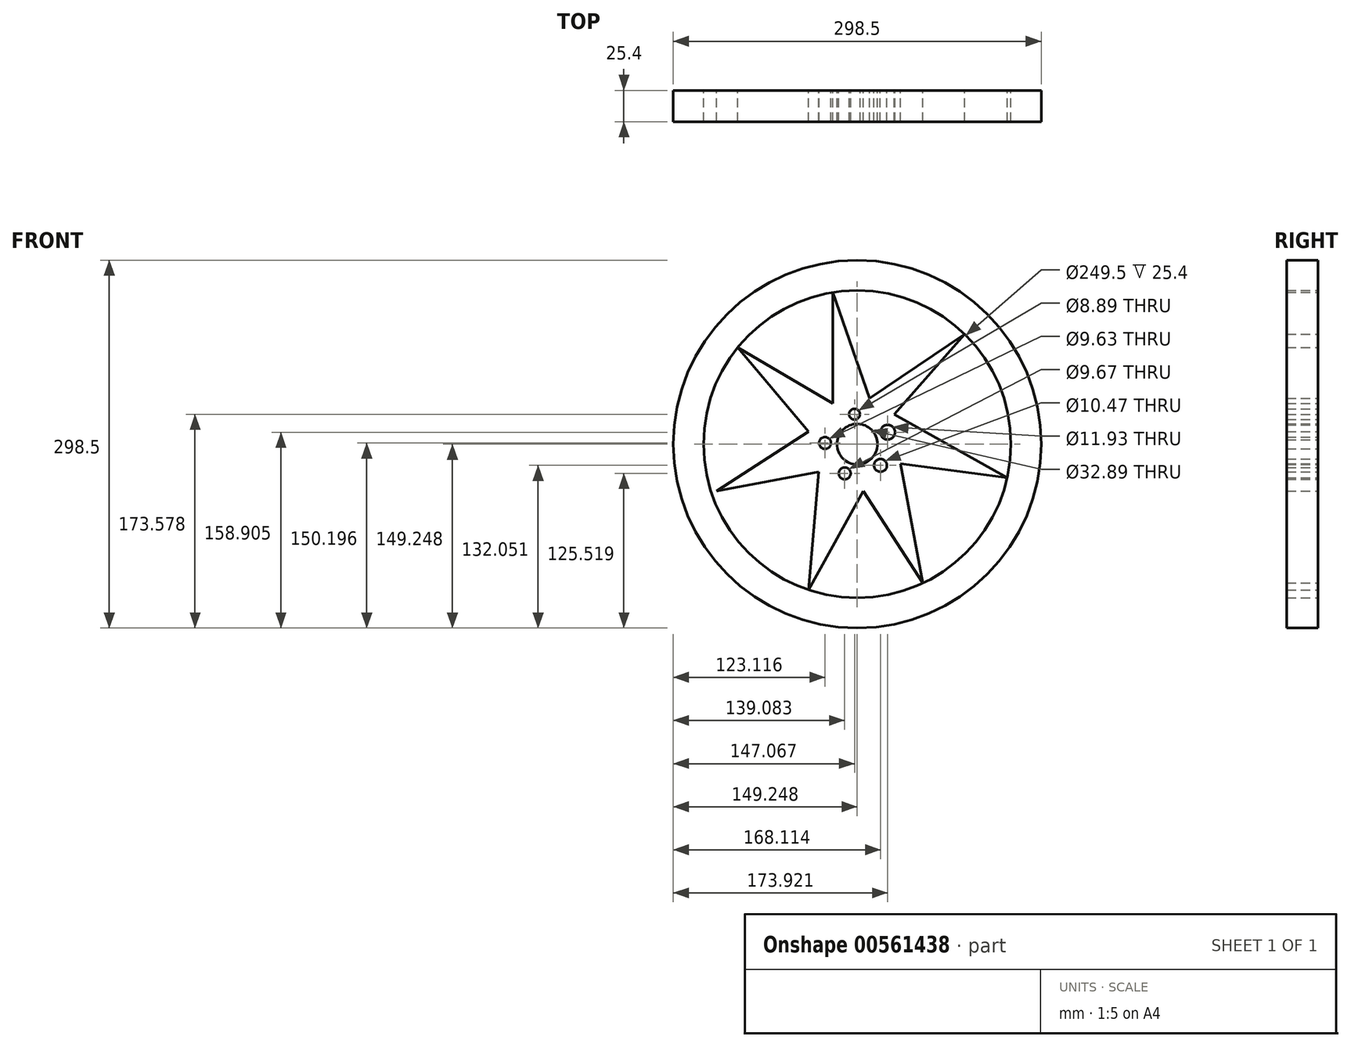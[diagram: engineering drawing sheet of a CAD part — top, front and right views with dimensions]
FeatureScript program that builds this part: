
annotation { "Feature Type Name" : "Feature", "Feature Type Description" : "" }
export const myFeature = defineFeature(function(context is Context, id is Id, definition is map)
    precondition{}
    {
        {
            var Q0;
            Q0=qCreatedBy(makeId("Front.planeOp"),FACE);
            var sketch = newSketch(context, id + "F0", { "sketchPlane" : qUnion([Q0])});
            skCircle(sketch, "E0", {"center": v(-96.48, 10) * mm, "radius": 149.25 * mm});
            skCircle(sketch, "E1", {"center": v(-96.48, 10) * mm, "radius": 141.67 * mm});
            skCircle(sketch, "E2", {"center": v(-96.48, 10) * mm, "radius": 124.75 * mm});
            skCircle(sketch, "E3", {"center": v(-96.48, 10) * mm, "radius": 38.51 * mm});
            skLineSegment(sketch, "E4", {"start": v(-66.63, 34.34) * mm, "end": v(25.26, -17.2) * mm});
            skLineSegment(sketch, "E5", {"start": v(25.26, -17.2) * mm, "end": v(-61.37, -5.82) * mm});
            skLineSegment(sketch, "E6", {"start": v(-61.37, -5.82) * mm, "end": v(-43.16, -102.77) * mm});
            skLineSegment(sketch, "E7", {"start": v(-43.16, -102.77) * mm, "end": v(-91.5, -28.18) * mm});
            skLineSegment(sketch, "E8", {"start": v(-91.5, -28.18) * mm, "end": v(-135.93, -108.34) * mm});
            skLineSegment(sketch, "E9", {"start": v(-135.93, -108.34) * mm, "end": v(-127.68, -12.58) * mm});
            skLineSegment(sketch, "E10", {"start": v(-127.68, -12.58) * mm, "end": v(-210.75, -28.18) * mm});
            skLineSegment(sketch, "E11", {"start": v(-210.75, -28.18) * mm, "end": v(-135.93, 20.3) * mm});
            skLineSegment(sketch, "E12", {"start": v(-135.93, 20.3) * mm, "end": v(-193.56, 88.36) * mm});
            skLineSegment(sketch, "E13", {"start": v(-193.56, 88.36) * mm, "end": v(-116.43, 42.95) * mm});
            skLineSegment(sketch, "E14", {"start": v(-116.43, 42.95) * mm, "end": v(-116.43, 133.15) * mm});
            skLineSegment(sketch, "E15", {"start": v(-116.43, 133.15) * mm, "end": v(-86.35, 47.17) * mm});
            skLineSegment(sketch, "E16", {"start": v(-66.63, 34.34) * mm, "end": v(-9.44, 99.38) * mm});
            skLineSegment(sketch, "E17", {"start": v(-9.44, 99.38) * mm, "end": v(-86.35, 47.17) * mm});
            skCircle(sketch, "E18", {"center": v(-96.48, 10) * mm, "radius": 16.44 * mm});
            skCircle(sketch, "E19", {"center": v(-98.66, 34.34) * mm, "radius": 4.44 * mm});
            skCircle(sketch, "E20", {"center": v(-122.61, 10.96) * mm, "radius": 4.81 * mm});
            skCircle(sketch, "E21", {"center": v(-106.65, -13.72) * mm, "radius": 4.84 * mm});
            skCircle(sketch, "E22", {"center": v(-77.62, -7.19) * mm, "radius": 5.23 * mm});
            skCircle(sketch, "E23", {"center": v(-71.8, 19.67) * mm, "radius": 5.97 * mm});
            skSolve(sketch);
        }
        {
            var Q0;
            Q0 = qSketchRegion(id + "F0", true);
            var Q1;
            {var subQ0=sQuery(id+"F0.wireOp",EDGE,"E10");Q1=makeQuery(id+"F0.imprint","IMPRINT",FACE,{"disambiguationData":[TD([[makeQuery(id+"F0.imprint","IMPRINT",EDGE,{"derivedFrom":subQ0}),-1.0]])]});}
            var Q2;
            Q2=makeQuery(id+"F0.imprint","IMPRINT",FACE,{"disambiguationData":[TD([[makeQuery(id+"F0.imprint","IMPRINT",EDGE,{"derivedFrom":sQuery(id+"F0.wireOp",EDGE,"E18")}),-1.0]])]});
            var Q3;
            {var subQ0=sQuery(id+"F0.wireOp",EDGE,"E16");Q3=makeQuery(id+"F0.imprint","IMPRINT",FACE,{"disambiguationData":[TD([[makeQuery(id+"F0.imprint","IMPRINT",EDGE,{"derivedFrom":subQ0}),1.0]])]});}
            var Q4;
            {var subQ0=sQuery(id+"F0.wireOp",EDGE,"E14");Q4=makeQuery(id+"F0.imprint","IMPRINT",FACE,{"disambiguationData":[TD([[makeQuery(id+"F0.imprint","IMPRINT",EDGE,{"derivedFrom":subQ0}),-1.0]])]});}
            var Q5;
            {var subQ0=sQuery(id+"F0.wireOp",EDGE,"E4");Q5=makeQuery(id+"F0.imprint","IMPRINT",FACE,{"disambiguationData":[TD([[makeQuery(id+"F0.imprint","IMPRINT",EDGE,{"derivedFrom":subQ0}),-1.0]])]});}
            var Q6;
            {var subQ0=sQuery(id+"F0.wireOp",EDGE,"E6");Q6=makeQuery(id+"F0.imprint","IMPRINT",FACE,{"disambiguationData":[TD([[makeQuery(id+"F0.imprint","IMPRINT",EDGE,{"derivedFrom":subQ0}),-1.0]])]});}
            var Q7;
            {var subQ0=sQuery(id+"F0.wireOp",EDGE,"E8");Q7=makeQuery(id+"F0.imprint","IMPRINT",FACE,{"disambiguationData":[TD([[makeQuery(id+"F0.imprint","IMPRINT",EDGE,{"derivedFrom":subQ0}),-1.0]])]});}
            extrude(context, id + "F1", {"entities" : qUnion([Q0, Q1, Q2, Q3, Q4, Q5, Q6, Q7]), "depth" : 25.4 * mm, "offsetDistance" : 25.4 * mm});
        }
        {
            var Q0;
            Q0=makeQuery(id+"F0.imprint","IMPRINT",FACE,{"disambiguationData":[TD([[makeQuery(id+"F0.imprint","IMPRINT",EDGE,{"derivedFrom":sQuery(id+"F0.wireOp",EDGE,"E1")}),1.0]])]});
            extrude(context, id + "F2", {"entities" : qUnion([Q0]), "operationType" : NewBodyOperationType.ADD, "depth" : 25.4 * mm, "offsetDistance" : 25.4 * mm});
        }
    });
